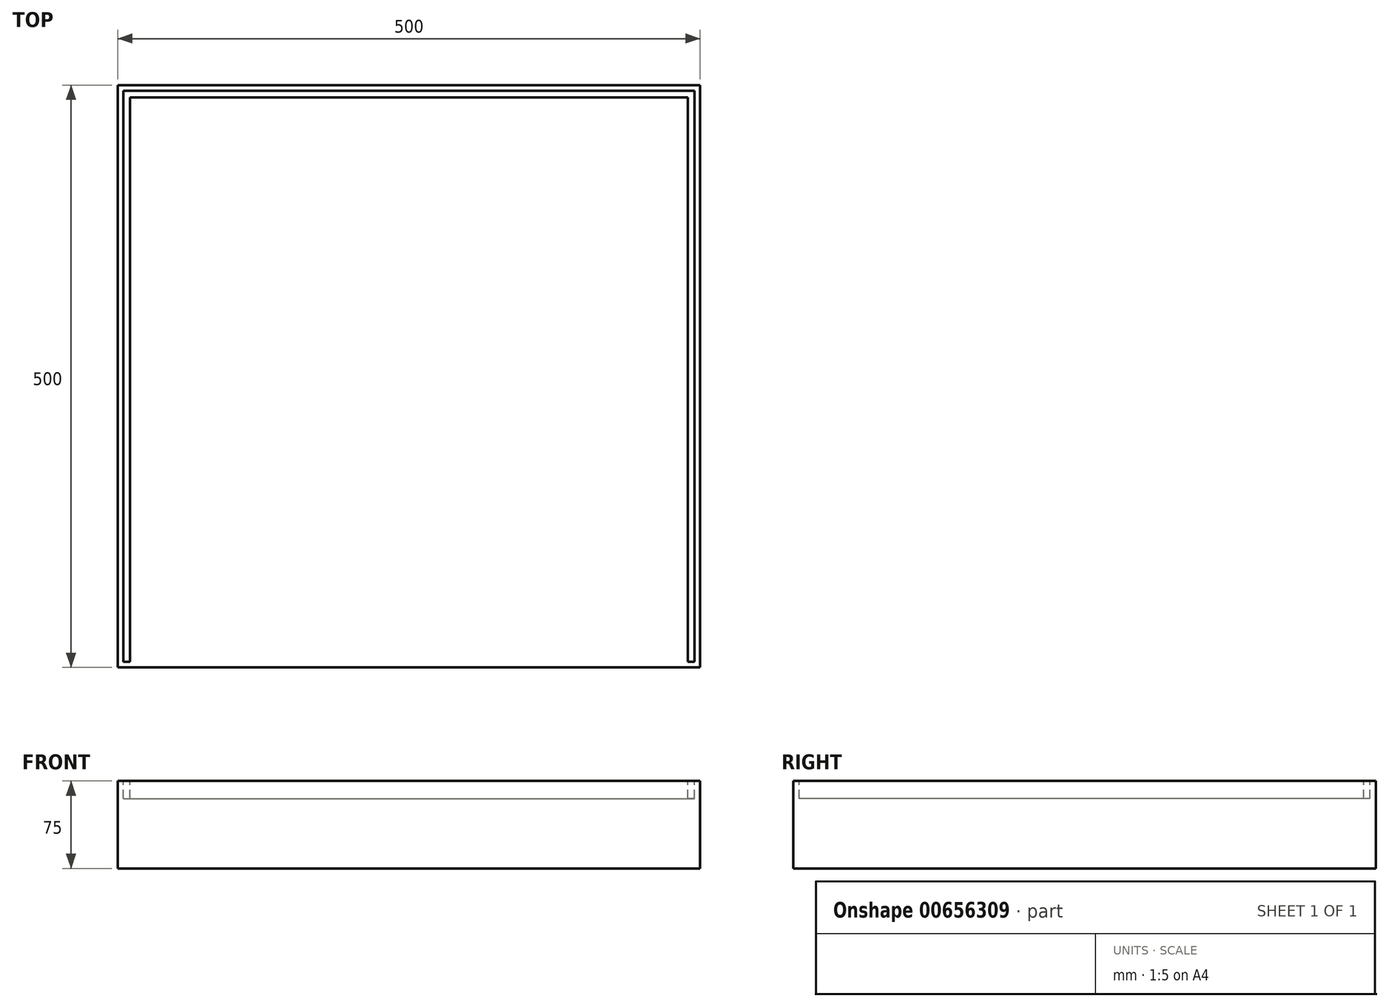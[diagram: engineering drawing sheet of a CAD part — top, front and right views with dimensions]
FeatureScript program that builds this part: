
annotation { "Feature Type Name" : "Feature", "Feature Type Description" : "" }
export const myFeature = defineFeature(function(context is Context, id is Id, definition is map)
    precondition{}
    {
        {
            var Q0;
            Q0=qCreatedBy(makeId("Top.planeOp"),FACE);
            var sketch = newSketch(context, id + "F0", { "sketchPlane" : qUnion([Q0])});
            skLineSegment(sketch, "E0.bottom", {"start": v(250, 250) * mm, "end": v(-250, 250) * mm});
            skLineSegment(sketch, "E0.top", {"start": v(250, -250) * mm, "end": v(-250, -250) * mm});
            skLineSegment(sketch, "E0.left", {"start": v(250, 250) * mm, "end": v(250, -250) * mm});
            skLineSegment(sketch, "E0.right", {"start": v(-250, 250) * mm, "end": v(-250, -250) * mm});
            skPoint(sketch, "E0.middle", {"position": v(0, 0) * mm});
            skSolve(sketch);
        }
        {
            var Q0;
            Q0 = qSketchRegion(id + "F0", true);
            extrude(context, id + "F1", {"entities" : qUnion([Q0]), "depth" : 75 * mm, "offsetDistance" : 25 * mm});
        }
        {
            var Q0;
            Q0=makeQuery(id+"F1.opExtrude","CAP_FACE",FACE,{"disambiguationData":[OSD([sQuery(id+"F0.wireOp",EDGE,"E0.bottom"),sQuery(id+"F0.wireOp",EDGE,"E0.top"),sQuery(id+"F0.wireOp",EDGE,"E0.left"),sQuery(id+"F0.wireOp",EDGE,"E0.right")])],"isStart":false});
            var sketch = newSketch(context, id + "F2", { "sketchPlane" : qUnion([Q0])});
            skLineSegment(sketch, "E1.bottom", {"start": v(-245, 245) * mm, "end": v(-239.5, 245) * mm});
            skLineSegment(sketch, "E1.top", {"start": v(-245, -245) * mm, "end": v(-239.5, -245) * mm});
            skLineSegment(sketch, "E1.left", {"start": v(-245, 245) * mm, "end": v(-245, -245) * mm});
            skLineSegment(sketch, "E1.right", {"start": v(-239.5, 245) * mm, "end": v(-239.5, -245) * mm});
            skLineSegment(sketch, "E2.MirrorCS", {"start": v(239.5, 245) * mm, "end": v(239.5, -245) * mm});
            skLineSegment(sketch, "E3.MirrorCS", {"start": v(245, 245) * mm, "end": v(245, -245) * mm});
            skLineSegment(sketch, "E4.MirrorCS", {"start": v(245, 245) * mm, "end": v(239.5, 245) * mm});
            skLineSegment(sketch, "E5.MirrorCS", {"start": v(245, -245) * mm, "end": v(239.5, -245) * mm});
            skLineSegment(sketch, "E6.bottom", {"start": v(-239.5, 245) * mm, "end": v(239.5, 245) * mm});
            skLineSegment(sketch, "E6.top", {"start": v(-239.5, 239.5) * mm, "end": v(239.5, 239.5) * mm});
            skLineSegment(sketch, "E6.left", {"start": v(-239.5, 245) * mm, "end": v(-239.5, 239.5) * mm});
            skLineSegment(sketch, "E6.right", {"start": v(239.5, 245) * mm, "end": v(239.5, 239.5) * mm});
            skSolve(sketch);
        }
        {
            var Q0;
            Q0=makeQuery(id+"F2.imprint","IMPRINT",FACE,{"disambiguationData":[TD([[makeQuery(id+"F2.imprint","IMPRINT",EDGE,{"derivedFrom":sQuery(id+"F2.wireOp",EDGE,"E1.bottom")}),-1.0]])]});
            var Q1;
            Q1=makeQuery(id+"F2.imprint","IMPRINT",FACE,{"disambiguationData":[TD([[makeQuery(id+"F2.imprint","IMPRINT",EDGE,{"derivedFrom":sQuery(id+"F2.wireOp",EDGE,"E2.MirrorCS")}),1.0]])]});
            var Q2;
            Q2=makeQuery(id+"F2.imprint","IMPRINT",FACE,{"disambiguationData":[TD([[makeQuery(id+"F2.imprint","IMPRINT",EDGE,{"derivedFrom":sQuery(id+"F2.wireOp",EDGE,"E6.bottom")}),-1.0]])]});
            extrude(context, id + "F3", {"entities" : qUnion([Q0, Q1, Q2]), "operationType" : NewBodyOperationType.REMOVE, "oppositeDirection" : true, "depth" : 15 * mm, "offsetDistance" : 25 * mm});
        }
    });
